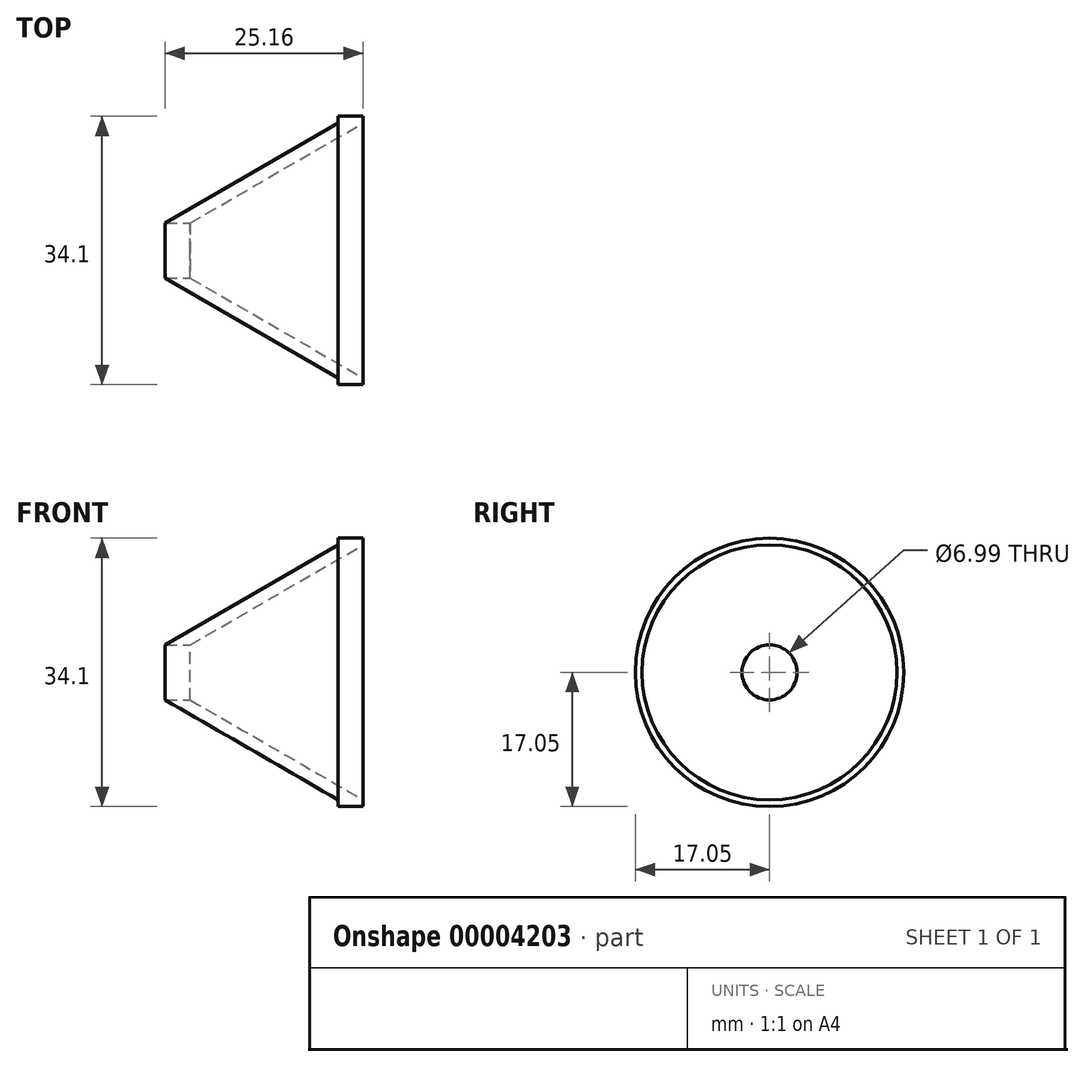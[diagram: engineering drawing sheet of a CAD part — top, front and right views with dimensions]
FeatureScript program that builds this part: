
annotation { "Feature Type Name" : "Feature", "Feature Type Description" : "" }
export const myFeature = defineFeature(function(context is Context, id is Id, definition is map)
    precondition{}
    {
        {
            var Q0;
            Q0=qCreatedBy(makeId("Front.planeOp"),FACE);
            var sketch = newSketch(context, id + "F0", { "sketchPlane" : qUnion([Q0])});
            skLineSegment(sketch, "E0", {"start": v(-1.97, 17.05) * mm, "end": v(-1.97, 16.19) * mm});
            skLineSegment(sketch, "E1", {"start": v(1.2, 16.19) * mm, "end": v(1.2, 17.05) * mm});
            skLineSegment(sketch, "E2", {"start": v(0, 0) * mm, "end": v(-25.22, 0) * mm});
            skLineSegment(sketch, "E3", {"start": v(-1.97, 17.05) * mm, "end": v(1.2, 17.05) * mm});
            skLineSegment(sketch, "E4", {"start": v(-23.96, 3.5) * mm, "end": v(-20.79, 3.5) * mm});
            skLineSegment(sketch, "E5", {"start": v(-1.97, 16.19) * mm, "end": v(-23.96, 3.5) * mm});
            skLineSegment(sketch, "E6", {"start": v(-20.79, 3.5) * mm, "end": v(1.2, 16.19) * mm});
            skSolve(sketch);
        }
        {
            var Q0;
            Q0=makeQuery(id+"F0.imprint","IMPRINT",FACE,{"disambiguationData":[TD([[makeQuery(id+"F0.imprint","IMPRINT",EDGE,{"derivedFrom":sQuery(id+"F0.wireOp",EDGE,"E0")}),1.0]])]});
            var Q1;
            Q1=sQuery(id+"F0.wireOp",EDGE,"E2");
            revolve(context, id + "F1", {"entities" : qUnion([Q0]), "axis" : qUnion([Q1]), "revolveType" : RevolveType.FULL});
        }
    });
